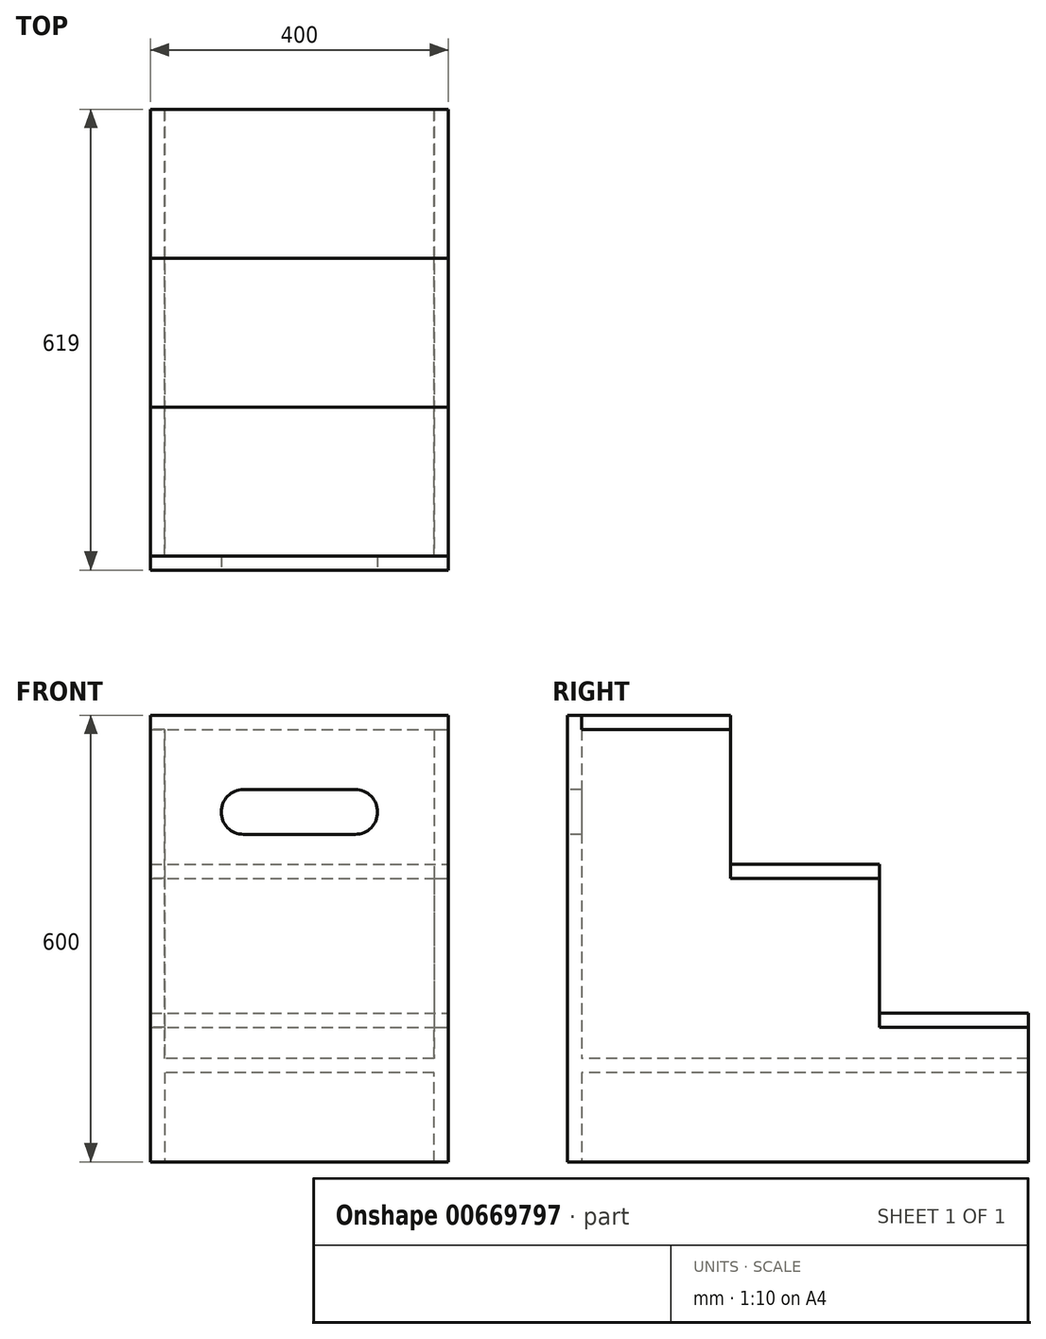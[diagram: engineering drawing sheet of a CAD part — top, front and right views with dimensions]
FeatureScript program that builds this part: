
annotation { "Feature Type Name" : "Feature", "Feature Type Description" : "" }
export const myFeature = defineFeature(function(context is Context, id is Id, definition is map)
    precondition{}
    {
        {
            var Q0;
            Q0=qCreatedBy(makeId("Right.planeOp"),FACE);
            var sketch = newSketch(context, id + "F0", { "sketchPlane" : qUnion([Q0])});
            skLineSegment(sketch, "E0", {"start": v(-400, 804.24) * mm, "end": v(-400, 204.24) * mm});
            skLineSegment(sketch, "E1", {"start": v(-400, 204.24) * mm, "end": v(200, 204.24) * mm});
            skLineSegment(sketch, "E2", {"start": v(200, 204.24) * mm, "end": v(200, 404.24) * mm});
            skLineSegment(sketch, "E3", {"start": v(200, 404.24) * mm, "end": v(0, 404.24) * mm});
            skLineSegment(sketch, "E4", {"start": v(0, 404.24) * mm, "end": v(0, 604.24) * mm});
            skLineSegment(sketch, "E5", {"start": v(0, 604.24) * mm, "end": v(-200, 604.24) * mm});
            skLineSegment(sketch, "E6", {"start": v(-200, 604.24) * mm, "end": v(-200, 804.24) * mm});
            skLineSegment(sketch, "E7", {"start": v(-200, 804.24) * mm, "end": v(-400, 804.24) * mm});
            skLineSegment(sketch, "E8", {"start": v(-400, 785.24) * mm, "end": v(-200, 785.24) * mm});
            skLineSegment(sketch, "E9", {"start": v(-200, 604.24) * mm, "end": v(-200, 585.24) * mm});
            skLineSegment(sketch, "E10", {"start": v(-200, 585.24) * mm, "end": v(0, 585.24) * mm});
            skLineSegment(sketch, "E11", {"start": v(0, 404.24) * mm, "end": v(0, 385.24) * mm});
            skLineSegment(sketch, "E12", {"start": v(0, 385.24) * mm, "end": v(200, 385.24) * mm});
            skSolve(sketch);
        }
        {
            var Q0;
            {var subQ1=sQuery(id+"F0.wireOp",EDGE,"E1");Q0=makeQuery(id+"F0.imprint","IMPRINT",FACE,{"disambiguationData":[TD([[makeQuery(id+"F0.imprint","IMPRINT",EDGE,{"derivedFrom":subQ1}),1.0]])]});}
            extrude(context, id + "F1", {"entities" : qUnion([Q0]), "oppositeDirection" : true, "depth" : 19 * mm, "offsetDistance" : 25 * mm});
        }
        {
            var Q0;
            {var subQ0=sQuery(id+"F0.wireOp",EDGE,"E7");Q0=makeQuery(id+"F0.imprint","IMPRINT",FACE,{"disambiguationData":[TD([[makeQuery(id+"F0.imprint","IMPRINT",EDGE,{"derivedFrom":subQ0}),1.0]])]});}
            var Q1;
            {var subQ0=sQuery(id+"F0.wireOp",EDGE,"E5");Q1=makeQuery(id+"F0.imprint","IMPRINT",FACE,{"disambiguationData":[TD([[makeQuery(id+"F0.imprint","IMPRINT",EDGE,{"derivedFrom":subQ0}),1.0]])]});}
            var Q2;
            {var subQ0=sQuery(id+"F0.wireOp",EDGE,"E3");Q2=makeQuery(id+"F0.imprint","IMPRINT",FACE,{"disambiguationData":[TD([[makeQuery(id+"F0.imprint","IMPRINT",EDGE,{"derivedFrom":subQ0}),1.0]])]});}
            extrude(context, id + "F2", {"entities" : qUnion([Q0, Q1, Q2]), "oppositeDirection" : true, "depth" : 400 * mm, "offsetDistance" : 25 * mm});
        }
        {
            var Q0;
            {var subQ1=sQuery(id+"F0.wireOp",EDGE,"E1");Q0=makeQuery(id+"F0.imprint","IMPRINT",FACE,{"disambiguationData":[TD([[makeQuery(id+"F0.imprint","IMPRINT",EDGE,{"derivedFrom":subQ1}),1.0]])]});}
            cPlane(context, id + "F3", {"entities" : qUnion([Q0]), "cplaneType" : CPlaneType.OFFSET, "offset" : 400 * mm, "oppositeDirection" : true, "width" : 150 * mm, "height" : 150 * mm});
        }
        {
            var Q0;
            Q0=qCreatedBy(id+"F3.planeOp",FACE);
            var sketch = newSketch(context, id + "F4", { "sketchPlane" : qUnion([Q0])});
            skLineSegment(sketch, "E13.0", {"start": v(-200, 604.24) * mm, "end": v(-200, 804.24) * mm});
            skLineSegment(sketch, "E14.0.0", {"start": v(-400, 785.24) * mm, "end": v(-200, 785.24) * mm});
            skLineSegment(sketch, "E14.0.1", {"start": v(-200, 785.24) * mm, "end": v(-200, 585.24) * mm});
            skLineSegment(sketch, "E14.0.2", {"start": v(-200, 585.24) * mm, "end": v(0, 585.24) * mm});
            skLineSegment(sketch, "E14.0.3", {"start": v(0, 585.24) * mm, "end": v(0, 385.24) * mm});
            skLineSegment(sketch, "E14.0.4", {"start": v(0, 385.24) * mm, "end": v(200, 385.24) * mm});
            skLineSegment(sketch, "E14.0.5", {"start": v(200, 385.24) * mm, "end": v(200, 204.24) * mm});
            skLineSegment(sketch, "E14.0.6", {"start": v(200, 204.24) * mm, "end": v(-400, 204.24) * mm});
            skLineSegment(sketch, "E14.0.7", {"start": v(-400, 204.24) * mm, "end": v(-400, 785.24) * mm});
            skLineSegment(sketch, "E15.0", {"start": v(-200, 804.24) * mm, "end": v(-400, 804.24) * mm});
            skLineSegment(sketch, "E16.0", {"start": v(-400, 804.24) * mm, "end": v(-400, 204.24) * mm});
            skLineSegment(sketch, "E17.0", {"start": v(0, 404.24) * mm, "end": v(0, 604.24) * mm});
            skLineSegment(sketch, "E18.0", {"start": v(0, 604.24) * mm, "end": v(-200, 604.24) * mm});
            skPoint(sketch, "E19.0", {"position": v(100, 404.24) * mm});
            skLineSegment(sketch, "E20.0", {"start": v(200, 204.24) * mm, "end": v(200, 404.24) * mm});
            skLineSegment(sketch, "E21.0", {"start": v(200, 404.24) * mm, "end": v(0, 404.24) * mm});
            skSolve(sketch);
        }
        {
            var Q0;
            {var subQ6=sQuery(id+"F4.wireOp",EDGE,"E14.0.0");Q0=makeQuery(id+"F4.imprint","IMPRINT",FACE,{"disambiguationData":[TD([[makeQuery(id+"F4.imprint","IMPRINT",EDGE,{"derivedFrom":subQ6}),-1.0]])]});}
            extrude(context, id + "F5", {"entities" : qUnion([Q0]), "depth" : 19 * mm, "offsetDistance" : 25 * mm});
        }
        {
            var Q0;
            Q0=makeQuery(id+"F2.opExtrude","SWEPT_FACE",FACE,{"disambiguationData":[OSD([sQuery(id+"F0.wireOp",EDGE,"E0")])]});
            var sketch = newSketch(context, id + "F6", { "sketchPlane" : qUnion([Q0])});
            skLineSegment(sketch, "E22.bottom", {"start": v(-400, 804.24) * mm, "end": v(0, 804.24) * mm});
            skLineSegment(sketch, "E22.top", {"start": v(-400, 204.24) * mm, "end": v(0, 204.24) * mm});
            skLineSegment(sketch, "E22.left", {"start": v(-400, 804.24) * mm, "end": v(-400, 204.24) * mm});
            skLineSegment(sketch, "E22.right", {"start": v(0, 804.24) * mm, "end": v(0, 204.24) * mm});
            skSolve(sketch);
        }
        {
            var Q0;
            {var subQ0=sQuery(id+"F6.wireOp",EDGE,"E22.bottom");Q0=makeQuery(id+"F6.imprint","IMPRINT",FACE,{"disambiguationData":[TD([[makeQuery(id+"F6.imprint","IMPRINT",EDGE,{"derivedFrom":subQ0}),-1.0]])]});}
            var Q1;
            {var subQ0=sQuery(id+"F6.wireOp",EDGE,"E22.top");Q1=makeQuery(id+"F6.imprint","IMPRINT",FACE,{"disambiguationData":[TD([[makeQuery(id+"F6.imprint","IMPRINT",EDGE,{"derivedFrom":subQ0}),1.0]])]});}
            extrude(context, id + "F7", {"entities" : qUnion([Q0, Q1]), "depth" : 19 * mm, "offsetDistance" : 25 * mm});
        }
        {
            var Q0;
            Q0=makeQuery(id+"F1.opExtrude","SWEPT_FACE",FACE,{"disambiguationData":[OSD([sQuery(id+"F0.wireOp",EDGE,"E1")])]});
            cPlane(context, id + "F8", {"entities" : qUnion([Q0]), "cplaneType" : CPlaneType.OFFSET, "offset" : 120 * mm, "oppositeDirection" : true, "width" : 150 * mm, "height" : 150 * mm});
        }
        {
            var Q0;
            Q0=qCreatedBy(id+"F8.planeOp",FACE);
            var sketch = newSketch(context, id + "F9", { "sketchPlane" : qUnion([Q0])});
            skLineSegment(sketch, "E23.bottom", {"start": v(-19, -200) * mm, "end": v(-381, -200) * mm});
            skLineSegment(sketch, "E23.top", {"start": v(-19, 400) * mm, "end": v(-381, 400) * mm});
            skLineSegment(sketch, "E23.left", {"start": v(-19, -200) * mm, "end": v(-19, 400) * mm});
            skLineSegment(sketch, "E23.right", {"start": v(-381, -200) * mm, "end": v(-381, 400) * mm});
            skSolve(sketch);
        }
        {
            var Q0;
            Q0=makeQuery(id+"F9.imprint","IMPRINT",FACE,{"disambiguationData":[TD([[makeQuery(id+"F9.imprint","IMPRINT",EDGE,{"derivedFrom":sQuery(id+"F9.wireOp",EDGE,"E23.bottom")}),-1.0]])]});
            extrude(context, id + "F10", {"entities" : qUnion([Q0]), "oppositeDirection" : true, "depth" : 19 * mm, "offsetDistance" : 25 * mm});
        }
        {
            var Q0;
            Q0=makeQuery(id+"F1.opExtrude","CAP_FACE",FACE,{"disambiguationData":[OSD([sQuery(id+"F0.wireOp",EDGE,"E0"),sQuery(id+"F0.wireOp",EDGE,"E1"),sQuery(id+"F0.wireOp",EDGE,"E2"),sQuery(id+"F0.wireOp",EDGE,"E4"),sQuery(id+"F0.wireOp",EDGE,"E6"),sQuery(id+"F0.wireOp",EDGE,"E8"),sQuery(id+"F0.wireOp",EDGE,"E9"),sQuery(id+"F0.wireOp",EDGE,"E10"),sQuery(id+"F0.wireOp",EDGE,"E11"),sQuery(id+"F0.wireOp",EDGE,"E12")])],"isStart":false});
            var sketch = newSketch(context, id + "F11", { "sketchPlane" : qUnion([Q0])});
            skLineSegment(sketch, "E24.bottom", {"start": v(-200, 343.24) * mm, "end": v(400, 343.24) * mm});
            skLineSegment(sketch, "E24.top", {"start": v(-200, 324.24) * mm, "end": v(400, 324.24) * mm});
            skLineSegment(sketch, "E24.left", {"start": v(-200, 343.24) * mm, "end": v(-200, 324.24) * mm});
            skLineSegment(sketch, "E24.right", {"start": v(400, 343.24) * mm, "end": v(400, 324.24) * mm});
            skSolve(sketch);
        }
        {
            var Q0;
            Q0=makeQuery(id+"F11.imprint","IMPRINT",FACE,{"disambiguationData":[TD([[makeQuery(id+"F11.imprint","IMPRINT",EDGE,{"derivedFrom":sQuery(id+"F11.wireOp",EDGE,"E24.bottom")}),-1.0]])]});
            extrude(context, id + "F12", {"entities" : qUnion([Q0]), "operationType" : NewBodyOperationType.REMOVE, "oppositeDirection" : true, "depth" : 5 * mm, "offsetDistance" : 25 * mm});
        }
        {
            var Q0;
            Q0=makeQuery(id+"F5.opExtrude","CAP_FACE",FACE,{"disambiguationData":[OSD([sQuery(id+"F4.wireOp",EDGE,"E14.0.0"),sQuery(id+"F4.wireOp",EDGE,"E14.0.1"),sQuery(id+"F4.wireOp",EDGE,"E14.0.2"),sQuery(id+"F4.wireOp",EDGE,"E14.0.3"),sQuery(id+"F4.wireOp",EDGE,"E14.0.4"),sQuery(id+"F4.wireOp",EDGE,"E14.0.6"),sQuery(id+"F4.wireOp",EDGE,"E16.0"),sQuery(id+"F4.wireOp",EDGE,"E17.0"),sQuery(id+"F4.wireOp",EDGE,"E20.0")])],"isStart":false});
            var sketch = newSketch(context, id + "F13", { "sketchPlane" : qUnion([Q0])});
            skLineSegment(sketch, "E25.bottom", {"start": v(-400, 343.24) * mm, "end": v(200, 343.24) * mm});
            skLineSegment(sketch, "E25.top", {"start": v(-400, 324.24) * mm, "end": v(200, 324.24) * mm});
            skLineSegment(sketch, "E25.left", {"start": v(-400, 343.24) * mm, "end": v(-400, 324.24) * mm});
            skLineSegment(sketch, "E25.right", {"start": v(200, 343.24) * mm, "end": v(200, 324.24) * mm});
            skSolve(sketch);
        }
        {
            var Q0;
            Q0=makeQuery(id+"F13.imprint","IMPRINT",FACE,{"disambiguationData":[TD([[makeQuery(id+"F13.imprint","IMPRINT",EDGE,{"derivedFrom":sQuery(id+"F13.wireOp",EDGE,"E25.bottom")}),-1.0]])]});
            extrude(context, id + "F14", {"entities" : qUnion([Q0]), "operationType" : NewBodyOperationType.REMOVE, "oppositeDirection" : true, "depth" : 5 * mm, "offsetDistance" : 25 * mm});
        }
        {
            var Q0;
            Q0=makeQuery(id+"F14.boolean.opBoolean","COPY",FACE,{"derivedFrom":makeQuery(id+"F14.opExtrude","CAP_FACE",FACE,{"disambiguationData":[OSD([sQuery(id+"F13.wireOp",EDGE,"E25.bottom"),sQuery(id+"F13.wireOp",EDGE,"E25.top"),sQuery(id+"F13.wireOp",EDGE,"E25.left"),sQuery(id+"F13.wireOp",EDGE,"E25.right")])],"isStart":false})});
            extrude(context, id + "F15", {"entities" : qUnion([Q0]), "operationType" : NewBodyOperationType.ADD, "endBound" : BoundingType.UP_TO_NEXT, "depth" : 25 * mm, "offsetDistance" : 25 * mm});
        }
        {
            var Q0;
            Q0=makeQuery(id+"F12.boolean.opBoolean","COPY",FACE,{"derivedFrom":makeQuery(id+"F12.opExtrude","CAP_FACE",FACE,{"disambiguationData":[OSD([sQuery(id+"F11.wireOp",EDGE,"E24.bottom"),sQuery(id+"F11.wireOp",EDGE,"E24.top"),sQuery(id+"F11.wireOp",EDGE,"E24.left"),sQuery(id+"F11.wireOp",EDGE,"E24.right")])],"isStart":false})});
            extrude(context, id + "F16", {"entities" : qUnion([Q0]), "operationType" : NewBodyOperationType.ADD, "endBound" : BoundingType.UP_TO_NEXT, "depth" : 25 * mm, "offsetDistance" : 25 * mm});
        }
        {
            var Q0;
            Q0=makeQuery(id+"F7.opExtrude","CAP_FACE",FACE,{"disambiguationData":[OSD([sQuery(id+"F6.wireOp",EDGE,"E22.bottom"),sQuery(id+"F6.wireOp",EDGE,"E22.top"),sQuery(id+"F6.wireOp",EDGE,"E22.left"),sQuery(id+"F6.wireOp",EDGE,"E22.right")])],"isStart":false});
            var sketch = newSketch(context, id + "F17", { "sketchPlane" : qUnion([Q0])});
            skLineSegment(sketch, "E26.bottom", {"start": v(-275, 704.24) * mm, "end": v(-125, 704.24) * mm});
            skLineSegment(sketch, "E26.top", {"start": v(-275, 644.24) * mm, "end": v(-125, 644.24) * mm});
            skLineSegment(sketch, "E26.left", {"start": v(-275, 704.24) * mm, "end": v(-275, 644.24) * mm});
            skLineSegment(sketch, "E26.right", {"start": v(-125, 704.24) * mm, "end": v(-125, 644.24) * mm});
            skLineSegment(sketch, "E27", {"start": v(-400, 674.24) * mm, "end": v(0, 674.24) * mm, "construction": true});
            skLineSegment(sketch, "E28", {"start": v(-200, 790.2) * mm, "end": v(-200, 674.24) * mm, "construction": true});
            skPoint(sketch, "E29", {"position": v(-275, 674.24) * mm});
            skPoint(sketch, "E30", {"position": v(-200, 704.24) * mm});
            skArc(sketch, "E31", {"start": v(-275, 704.24) * mm, "mid": v(-305, 674.24) * mm, "end": v(-275, 644.24) * mm});
            skArc(sketch, "E32", {"start": v(-125, 644.24) * mm, "mid": v(-95, 674.24) * mm, "end": v(-125, 704.24) * mm});
            skSolve(sketch);
        }
        {
            var Q0;
            Q0=makeQuery(id+"F17.imprint","IMPRINT",FACE,{"disambiguationData":[TD([[makeQuery(id+"F17.imprint","IMPRINT",EDGE,{"derivedFrom":sQuery(id+"F17.wireOp",EDGE,"E26.bottom")}),-1.0]])]});
            var Q1;
            Q1=makeQuery(id+"F17.imprint","IMPRINT",FACE,{"disambiguationData":[TD([[makeQuery(id+"F17.imprint","IMPRINT",EDGE,{"derivedFrom":sQuery(id+"F17.wireOp",EDGE,"E26.left")}),-1.0]])]});
            var Q2;
            Q2=makeQuery(id+"F17.imprint","IMPRINT",FACE,{"disambiguationData":[TD([[makeQuery(id+"F17.imprint","IMPRINT",EDGE,{"derivedFrom":sQuery(id+"F17.wireOp",EDGE,"E26.right")}),1.0]])]});
            extrude(context, id + "F18", {"entities" : qUnion([Q0, Q1, Q2]), "operationType" : NewBodyOperationType.REMOVE, "oppositeDirection" : true, "depth" : 25 * mm, "offsetDistance" : 25 * mm});
        }
    });
